# Revit family: Reece_Basin_Alape_Circa_Freestanding Basin_404 mm_Wall Attached
name_source: partatom
category: Plumbing Fixtures
revit_build: Autodesk Revit 2018 (Build: 20180329_1100(x64)
units: mm (PartAtom-declared; Revit-internal decimal feet)

## family parameters
Always vertical = Yes
Cut with Voids When Loaded = Yes
Part Type = Normal
Room Calculation Point = Yes
Round Connector Dimension = Use Diameter
Shared = Yes
Work Plane-Based = Yes

## types (2) — shared parameters
Disclaimer = THIS FILE IS THE PROPERTY OF THE REECE GROUP. IT MAY NOT BE REPRODUCED, REVERSE-ENGINEERED OR MODIFIED. ANY REPUBLICATION, TRANSMISSION OR DISTRIBUTION FOR THE PURPOSE OF COMMERCIALLY EXPLOITING THE FILES IS PROHIBITED.
Manufacturer = Alape
Model = Circa
Reece_Basin_Height = 135 mm  [stored 0.442913 ft]
Reece_Basin_Outlet = 32 mm  [stored 0.104987 ft]
Reece_Detail_Additional = Wall Attached
Reece_Detail_Connector = No Taphole
Reece_Detail_Installation = Freestanding Basin
Reece_Overall_Capacity = 7 L
Reece_Overall_Height = 900 mm  [stored 2.95276 ft]
Reece_Overall_Length = 444 mm
Reece_Overall_Width = 404 mm  [stored 1.32546 ft]
Reece_Product_Brand = Alape
Reece_Product_Mount = Wall Mounted
Reece_Product_Sub Brand = Circa
Reece_Product_Type = Basin
Reece_Product_Web Page = https://www.reece.com.au
Type Comments = Basin
URL = https://www.reece.com.au
zero-valued in all types: Default Elevation

## per-type parameters (varying)
| type | Description | Keynote | Reece_Material_Main | Reece_Product_Description | Reece_Product_Number |
| 7 L_Enamelled Glazed Steel_Dark Iron | Alape Circa Freestanding Basin 400mm Dark Iron (Wall Attached) | Product #9508139, Reece_Basin_Alape_Circa_Freestanding Basin_404 mm_Wall Attached - 7 L_Enamelled Glazed Steel_Dark Iron | Reece_Metal_Glazed Steel_Dark Iron | Alape Circa Freestanding Basin 400mm Dark Iron (Wall Attached) | 9508139 |
| 7 L_Enamelled Glazed Steel_White | Alape Circa Freestanding Basin 400mm White (Wall Attached) | Product #9502690, Reece_Basin_Alape_Circa_Freestanding Basin_404 mm_Wall Attached - 7 L_Enamelled Glazed Steel_White | Reece_Metal_Glazed Steel_White | Alape Circa Freestanding Basin 400mm White (Wall Attached) | 9502690 |

note: [stored X ft] marks values corroborated as IEEE doubles in the binary element streams (Revit-internal decimal feet)

## geometry (parser evidence)
native form markers: Sweep x2
no freeform markers — native parametric forms only
